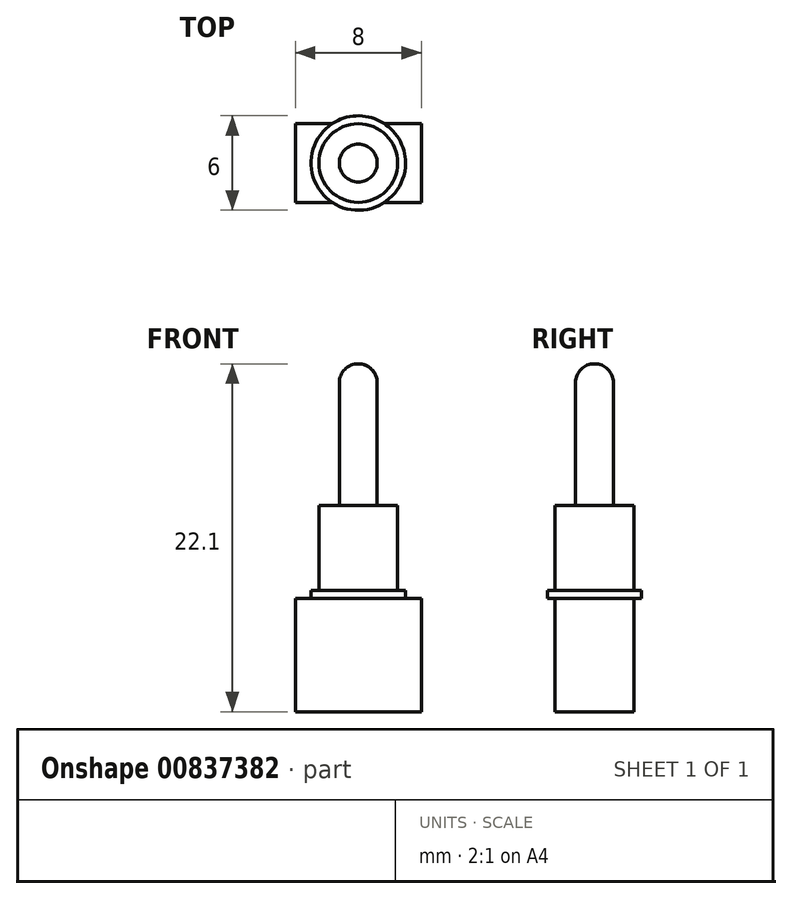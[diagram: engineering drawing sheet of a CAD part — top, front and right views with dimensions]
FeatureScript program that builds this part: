
annotation { "Feature Type Name" : "Feature", "Feature Type Description" : "" }
export const myFeature = defineFeature(function(context is Context, id is Id, definition is map)
    precondition{}
    {
        {
            var Q0;
            Q0=qCreatedBy(makeId("Top.planeOp"),FACE);
            var sketch = newSketch(context, id + "F0", { "sketchPlane" : qUnion([Q0])});
            skLineSegment(sketch, "E0.bottom", {"start": v(4, -2.5) * mm, "end": v(-4, -2.5) * mm});
            skLineSegment(sketch, "E0.top", {"start": v(4, 2.5) * mm, "end": v(-4, 2.5) * mm});
            skLineSegment(sketch, "E0.left", {"start": v(4, -2.5) * mm, "end": v(4, 2.5) * mm});
            skLineSegment(sketch, "E0.right", {"start": v(-4, -2.5) * mm, "end": v(-4, 2.5) * mm});
            skPoint(sketch, "E0.middle", {"position": v(0, 0) * mm});
            skSolve(sketch);
        }
        {
            var Q0;
            Q0 = qSketchRegion(id + "F0", true);
            extrude(context, id + "F1", {"entities" : qUnion([Q0]), "depth" : 7.2 * mm, "offsetDistance" : 25 * mm});
        }
        {
            var Q0;
            Q0=makeQuery(id+"F1.opExtrude","CAP_FACE",FACE,{"disambiguationData":[OSD([sQuery(id+"F0.wireOp",EDGE,"E0.bottom"),sQuery(id+"F0.wireOp",EDGE,"E0.top"),sQuery(id+"F0.wireOp",EDGE,"E0.left"),sQuery(id+"F0.wireOp",EDGE,"E0.right")])],"isStart":false});
            var sketch = newSketch(context, id + "F2", { "sketchPlane" : qUnion([Q0])});
            skCircle(sketch, "E1", {"center": v(0, 0) * mm, "radius": 3 * mm});
            skSolve(sketch);
        }
        {
            var Q0;
            Q0 = qSketchRegion(id + "F2", true);
            extrude(context, id + "F3", {"entities" : qUnion([Q0]), "operationType" : NewBodyOperationType.ADD, "depth" : 0.5 * mm, "offsetDistance" : 25 * mm});
        }
        {
            var Q0;
            Q0=makeQuery(id+"F3.opExtrude","CAP_FACE",FACE,{"disambiguationData":[OSD([sQuery(id+"F2.wireOp",EDGE,"E1")])],"isStart":false});
            var sketch = newSketch(context, id + "F4", { "sketchPlane" : qUnion([Q0])});
            skCircle(sketch, "E2", {"center": v(0, 0) * mm, "radius": 2.5 * mm});
            skSolve(sketch);
        }
        {
            var Q0;
            Q0 = qSketchRegion(id + "F4", true);
            extrude(context, id + "F5", {"entities" : qUnion([Q0]), "operationType" : NewBodyOperationType.ADD, "depth" : 5.4 * mm, "offsetDistance" : 25 * mm});
        }
        {
            var Q0;
            Q0=makeQuery(id+"F5.opExtrude","CAP_FACE",FACE,{"disambiguationData":[OSD([sQuery(id+"F4.wireOp",EDGE,"E2")])],"isStart":false});
            var sketch = newSketch(context, id + "F6", { "sketchPlane" : qUnion([Q0])});
            skCircle(sketch, "E3", {"center": v(0, 0) * mm, "radius": 1.2 * mm});
            skSolve(sketch);
        }
        {
            var Q0;
            Q0 = qSketchRegion(id + "F6", true);
            extrude(context, id + "F7", {"entities" : qUnion([Q0]), "operationType" : NewBodyOperationType.ADD, "depth" : 9 * mm, "offsetDistance" : 25 * mm});
        }
        {
            var Q0;
            Q0=makeQuery(id+"F7.opExtrude","CAP_EDGE",EDGE,{"disambiguationData":[OSD([sQuery(id+"F6.wireOp",EDGE,"E3")])],"isStart":false});
            fillet(context, id + "F8", {"entities" : qUnion([Q0]), "radius" : 1.2 * mm, "tangentPropagation" : true, "allowEdgeOverflow" : false});
        }
    });
